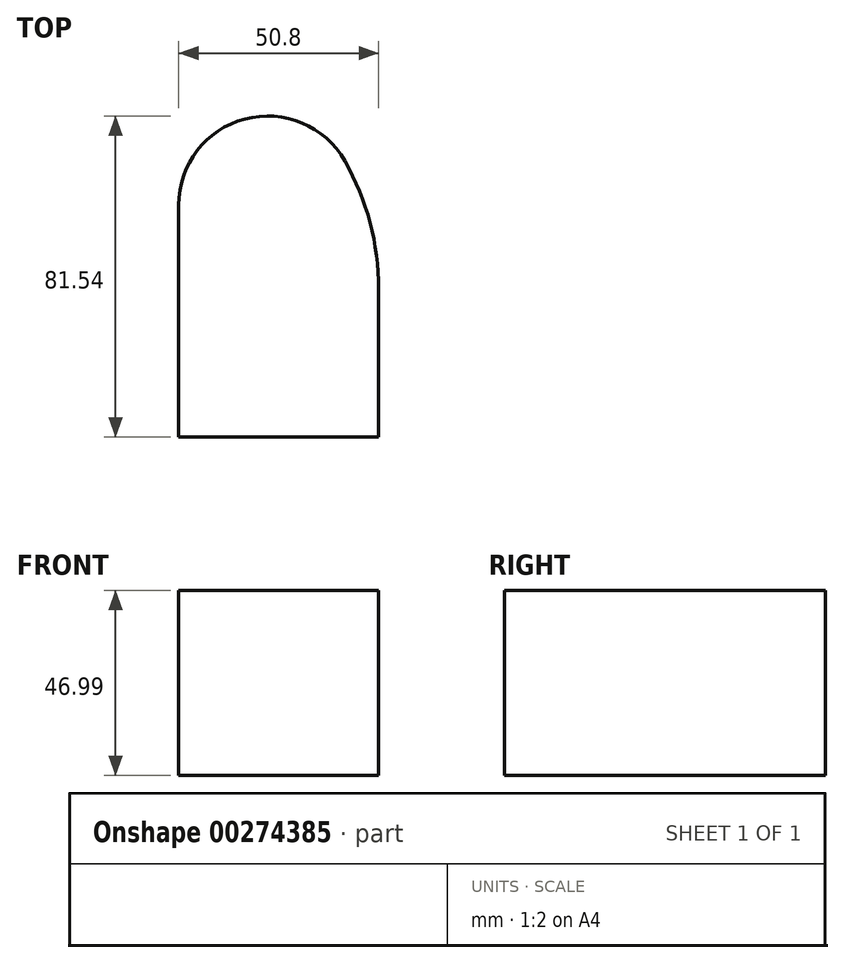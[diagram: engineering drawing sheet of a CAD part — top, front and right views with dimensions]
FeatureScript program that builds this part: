
annotation { "Feature Type Name" : "Feature", "Feature Type Description" : "" }
export const myFeature = defineFeature(function(context is Context, id is Id, definition is map)
    precondition{}
    {
        {
            var Q0;
            Q0=qCreatedBy(makeId("Top.planeOp"),FACE);
            var sketch = newSketch(context, id + "F0", { "sketchPlane" : qUnion([Q0])});
            skLineSegment(sketch, "E0.bottom", {"start": v(62.41, 41.35) * mm, "end": v(113.21, 41.35) * mm});
            skLineSegment(sketch, "E0.top", {"start": v(62.41, -60.25) * mm, "end": v(113.21, -60.25) * mm});
            skLineSegment(sketch, "E0.left", {"start": v(62.41, 41.35) * mm, "end": v(62.41, -60.25) * mm});
            skLineSegment(sketch, "E0.right", {"start": v(113.21, 41.35) * mm, "end": v(113.21, -60.25) * mm});
            skSolve(sketch);
        }
        {
            var Q0;
            Q0 = qSketchRegion(id + "F0", true);
            extrude(context, id + "F1", {"entities" : qUnion([Q0]), "depth" : 47 * mm});
        }
        {
            var Q0;
            Q0=makeQuery(id+"F1.opExtrude","SWEPT_EDGE",EDGE,{"disambiguationData":[OSD([sQuery(id+"F0.wireOp",EDGE,"E0.bottom"),sQuery(id+"F0.wireOp",EDGE,"E0.right")])]});
            fillet(context, id + "F2", {"entities" : qUnion([Q0]), "radius" : 65.61 * mm, "tangentPropagation" : true, "allowEdgeOverflow" : false});
        }
        {
            var Q0;
            Q0=makeQuery(id+"F2.opFillet","BLEND_EDGE",EDGE,{"blendedFrom":[makeQuery(id+"F1.opExtrude","SWEPT_EDGE",EDGE,{"disambiguationData":[OSD([sQuery(id+"F0.wireOp",EDGE,"E0.bottom"),sQuery(id+"F0.wireOp",EDGE,"E0.right")])]}),makeQuery(id+"F1.opExtrude","SWEPT_FACE",FACE,{"disambiguationData":[OSD([sQuery(id+"F0.wireOp",EDGE,"E0.left")])]})],"blendedInto":[makeQuery(id+"F1.opExtrude","SWEPT_FACE",FACE,{"disambiguationData":[OSD([sQuery(id+"F0.wireOp",EDGE,"E0.left")])]})]});
            fillet(context, id + "F3", {"entities" : qUnion([Q0]), "radius" : 22.59 * mm, "tangentPropagation" : true, "allowEdgeOverflow" : false});
        }
    });
